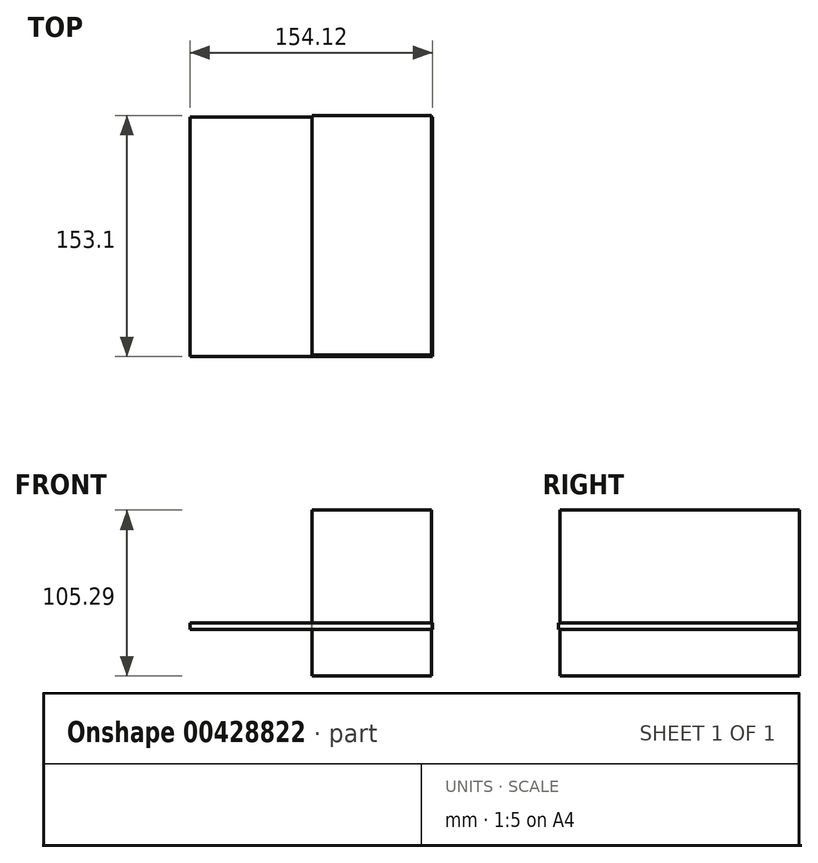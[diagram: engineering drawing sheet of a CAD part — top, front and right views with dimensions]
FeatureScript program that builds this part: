
annotation { "Feature Type Name" : "Feature", "Feature Type Description" : "" }
export const myFeature = defineFeature(function(context is Context, id is Id, definition is map)
    precondition{}
    {
        {
            var Q0;
            Q0=qCreatedBy(makeId("Top.planeOp"),FACE);
            var sketch = newSketch(context, id + "F0", { "sketchPlane" : qUnion([Q0])});
            skLineSegment(sketch, "E0.bottom", {"start": v(76.46, -77.04) * mm, "end": v(-77.66, -77.04) * mm});
            skLineSegment(sketch, "E0.top", {"start": v(76.46, 75.25) * mm, "end": v(-77.66, 75.25) * mm});
            skLineSegment(sketch, "E0.left", {"start": v(76.46, -77.04) * mm, "end": v(76.46, 75.25) * mm});
            skLineSegment(sketch, "E0.right", {"start": v(-77.66, -77.04) * mm, "end": v(-77.66, 75.25) * mm});
            skSolve(sketch);
        }
        {
            var Q0;
            Q0=makeQuery(id+"F0.imprint","IMPRINT",FACE,{"disambiguationData":[TD([[makeQuery(id+"F0.imprint","IMPRINT",EDGE,{"derivedFrom":sQuery(id+"F0.wireOp",EDGE,"E0.bottom")}),-1.0]])]});
            extrude(context, id + "F1", {"entities" : qUnion([Q0]), "depth" : 4.32 * mm});
        }
        {
            var Q0;
            Q0=qCreatedBy(makeId("Right.planeOp"),FACE);
            var sketch = newSketch(context, id + "F2", { "sketchPlane" : qUnion([Q0])});
            skLineSegment(sketch, "E1.bottom", {"start": v(-76.05, 75.85) * mm, "end": v(76.06, 75.85) * mm});
            skLineSegment(sketch, "E1.top", {"start": v(-76.05, 0) * mm, "end": v(76.06, 0) * mm});
            skLineSegment(sketch, "E1.left", {"start": v(-76.05, 75.85) * mm, "end": v(-76.05, 0) * mm});
            skLineSegment(sketch, "E1.right", {"start": v(76.06, 75.85) * mm, "end": v(76.06, 0) * mm});
            skSolve(sketch);
        }
        {
            var Q0;
            Q0 = qSketchRegion(id + "F2", true);
            extrude(context, id + "F3", {"entities" : qUnion([Q0]), "operationType" : NewBodyOperationType.ADD, "depth" : 25.4 * mm});
        }
        {
            var Q0;
            Q0=makeQuery(id+"F3.opExtrude","SWEPT_FACE",FACE,{"disambiguationData":[OSD([sQuery(id+"F2.wireOp",EDGE,"E1.bottom")])]});
            extrude(context, id + "F4", {"entities" : qUnion([Q0]), "operationType" : NewBodyOperationType.ADD, "oppositeDirection" : true, "depth" : 105.3 * mm});
        }
        {
            var Q0;
            {var subQ0=sQuery(id+"F2.wireOp",EDGE,"E1.bottom");Q0=makeQuery(id+"F4.boolean.opBoolean","MERGE",FACE,{"derivedFrom":[makeQuery(id+"F3.opExtrude","CAP_FACE",FACE,{"disambiguationData":[OSD([subQ0,sQuery(id+"F2.wireOp",EDGE,"E1.top"),sQuery(id+"F2.wireOp",EDGE,"E1.left"),sQuery(id+"F2.wireOp",EDGE,"E1.right")])],"isStart":true}),makeQuery(id+"F4.opExtrude","SWEPT_FACE",FACE,{"disambiguationData":[OSD([subQ0]),TDD([makeQuery(id+"F3.opExtrude","CAP_EDGE",EDGE,{"disambiguationData":[OSD([subQ0])],"isStart":true})])]})]});}
            extrude(context, id + "F5", {"entities" : qUnion([Q0]), "operationType" : NewBodyOperationType.ADD, "oppositeDirection" : true, "depth" : 75.8 * mm});
        }
    });
